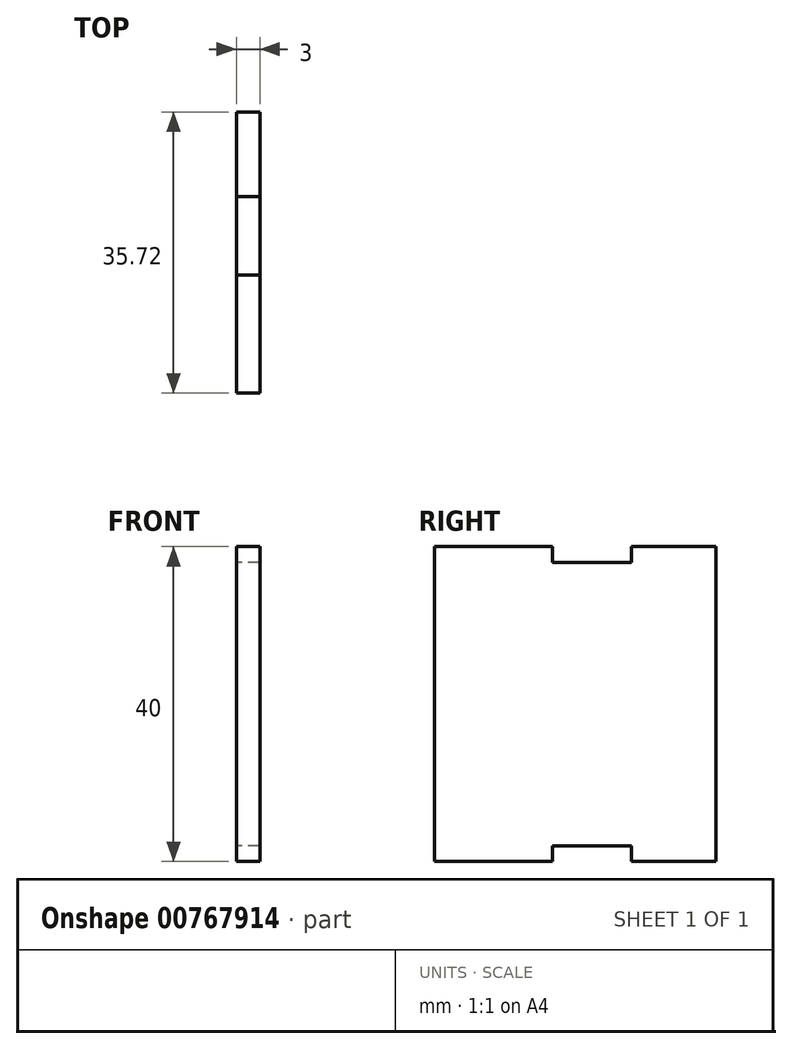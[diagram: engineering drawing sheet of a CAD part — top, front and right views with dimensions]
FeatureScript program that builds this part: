
annotation { "Feature Type Name" : "Feature", "Feature Type Description" : "" }
export const myFeature = defineFeature(function(context is Context, id is Id, definition is map)
    precondition{}
    {
        {
            var Q0;
            Q0=qCreatedBy(makeId("Right.planeOp"),FACE);
            var sketch = newSketch(context, id + "F0", { "sketchPlane" : qUnion([Q0])});
            skLineSegment(sketch, "E0.bottom", {"start": v(0, 0) * mm, "end": v(15, 0) * mm});
            skLineSegment(sketch, "E0.top", {"start": v(0, 40) * mm, "end": v(15, 40) * mm});
            skLineSegment(sketch, "E0.left", {"start": v(0, 0) * mm, "end": v(0, 40) * mm});
            skLineSegment(sketch, "E0.right", {"start": v(35.72, 0) * mm, "end": v(35.72, 40) * mm});
            skLineSegment(sketch, "E1.0", {"start": v(15, 0) * mm, "end": v(15, 2) * mm});
            skLineSegment(sketch, "E2.0", {"start": v(25, 0) * mm, "end": v(25, 2) * mm});
            skLineSegment(sketch, "E3", {"start": v(15, 38) * mm, "end": v(25, 38) * mm});
            skLineSegment(sketch, "E4", {"start": v(15, 2) * mm, "end": v(25, 2) * mm});
            skLineSegment(sketch, "E5.trimOffspring", {"start": v(25, 40) * mm, "end": v(35.72, 40) * mm});
            skLineSegment(sketch, "E6.trimOffspring", {"start": v(25, 0) * mm, "end": v(35.72, 0) * mm});
            skLineSegment(sketch, "E7.trimOffspring", {"start": v(15, 38) * mm, "end": v(15, 40) * mm});
            skLineSegment(sketch, "E8.trimOffspring", {"start": v(25, 38) * mm, "end": v(25, 40) * mm});
            skSolve(sketch);
        }
        {
            var Q0;
            Q0=makeQuery(id+"F0.imprint","IMPRINT",FACE,{"disambiguationData":[TD([[makeQuery(id+"F0.imprint","IMPRINT",EDGE,{"derivedFrom":sQuery(id+"F0.wireOp",EDGE,"E0.bottom")}),1.0]])]});
            extrude(context, id + "F1", {"entities" : qUnion([Q0]), "depth" : 3 * mm, "offsetDistance" : 25 * mm});
        }
    });
